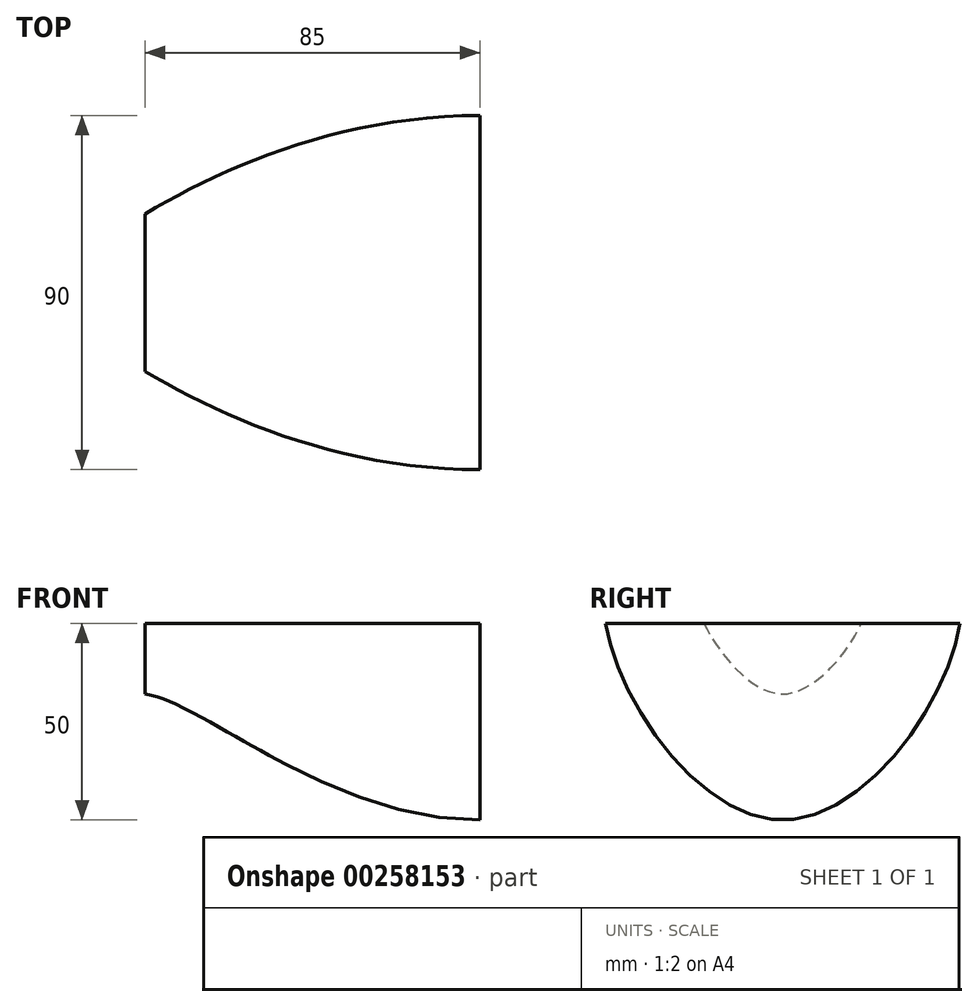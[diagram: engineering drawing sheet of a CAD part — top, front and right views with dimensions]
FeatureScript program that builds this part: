
annotation { "Feature Type Name" : "Feature", "Feature Type Description" : "" }
export const myFeature = defineFeature(function(context is Context, id is Id, definition is map)
    precondition{}
    {
        {
            var Q0;
            Q0=qCreatedBy(makeId("Right.planeOp"),FACE);
            var sketch = newSketch(context, id + "F0", { "sketchPlane" : qUnion([Q0])});
            skFitSpline(sketch, "E0", {"points": [v(-45, 0) * mm, v(0, -50) * mm, v(45, 0) * mm], "startDerivative": vector(18, -120) * mm, "endDerivative": vector(18, 120) * mm});
            skLineSegment(sketch, "E1", {"start": v(-45, 0) * mm, "end": v(0, 0) * mm});
            skLineSegment(sketch, "E2", {"start": v(0, 0) * mm, "end": v(45, 0) * mm});
            skSolve(sketch);
        }
        {
            var Q0;
            Q0=qCreatedBy(makeId("Right.planeOp"),FACE);
            cPlane(context, id + "F1", {"entities" : qUnion([Q0]), "cplaneType" : CPlaneType.OFFSET, "offset" : 85 * mm, "oppositeDirection" : true, "width" : 150 * mm, "height" : 150 * mm});
        }
        {
            var Q0;
            Q0=qCreatedBy(id+"F1.planeOp",FACE);
            var sketch = newSketch(context, id + "F2", { "sketchPlane" : qUnion([Q0])});
            skFitSpline(sketch, "E3", {"points": [v(-20, 0) * mm, v(0, -18) * mm, v(20, 0) * mm], "startDerivative": vector(12, -30) * mm, "endDerivative": vector(12, 30) * mm});
            skLineSegment(sketch, "E4", {"start": v(-20, 0) * mm, "end": v(0, 0) * mm});
            skLineSegment(sketch, "E5", {"start": v(0, 0) * mm, "end": v(20, 0) * mm});
            skSolve(sketch);
        }
        {
            var Q0;
            Q0=qCreatedBy(makeId("Top.planeOp"),FACE);
            var sketch = newSketch(context, id + "F3", { "sketchPlane" : qUnion([Q0])});
            skFitSpline(sketch, "E6", {"points": [v(-85, 20) * mm, v(0, 45) * mm], "startDerivative": vector(60, 36) * mm, "endDerivative": vector(105, 0) * mm});
            skSolve(sketch);
        }
        {
            var Q0;
            Q0=qCreatedBy(makeId("Top.planeOp"),FACE);
            var sketch = newSketch(context, id + "F4", { "sketchPlane" : qUnion([Q0])});
            skFitSpline(sketch, "E7", {"points": [v(-85, -20) * mm, v(0, -45) * mm], "startDerivative": vector(60, -36) * mm, "endDerivative": vector(105, 0) * mm});
            skSolve(sketch);
        }
        {
            var Q0;
            Q0=qCreatedBy(makeId("Front.planeOp"),FACE);
            var sketch = newSketch(context, id + "F5", { "sketchPlane" : qUnion([Q0])});
            skFitSpline(sketch, "E8", {"points": [v(-85, -18) * mm, v(0, -50) * mm], "startDerivative": vector(45, -6) * mm, "endDerivative": vector(115.32, 0) * mm});
            skSolve(sketch);
        }
        {
            var Q0;
            Q0=makeQuery(id+"F0.imprint","IMPRINT",FACE,{"disambiguationData":[TD([[makeQuery(id+"F0.imprint","IMPRINT",EDGE,{"derivedFrom":sQuery(id+"F0.wireOp",EDGE,"E0")}),1.0]])]});
            var Q1;
            Q1=makeQuery(id+"F2.imprint","IMPRINT",FACE,{"disambiguationData":[TD([[makeQuery(id+"F2.imprint","IMPRINT",EDGE,{"derivedFrom":sQuery(id+"F2.wireOp",EDGE,"E3")}),1.0]])]});
            var Q2;
            Q2=sQuery(id+"F4.wireOp",EDGE,"E7");
            var Q3;
            Q3=sQuery(id+"F5.wireOp",EDGE,"E8");
            var Q4;
            Q4=sQuery(id+"F3.wireOp",EDGE,"E6");
            loft(context, id + "F6", {"addGuides" : true, "sheetProfilesArray" : [{ "sheetProfileEntities" : qUnion([Q0]) }, { "sheetProfileEntities" : qUnion([Q1]) }], "guidesArray" : [{ "guideEntities" : qUnion([Q2]), "guideDerivativeType" : LoftGuideDerivativeType.DEFAULT, "guideDerivativeMagnitude" : 1 }, { "guideEntities" : qUnion([Q3]), "guideDerivativeType" : LoftGuideDerivativeType.DEFAULT, "guideDerivativeMagnitude" : 1 }, { "guideEntities" : qUnion([Q4]), "guideDerivativeType" : LoftGuideDerivativeType.DEFAULT, "guideDerivativeMagnitude" : 1 }]});
        }
    });
